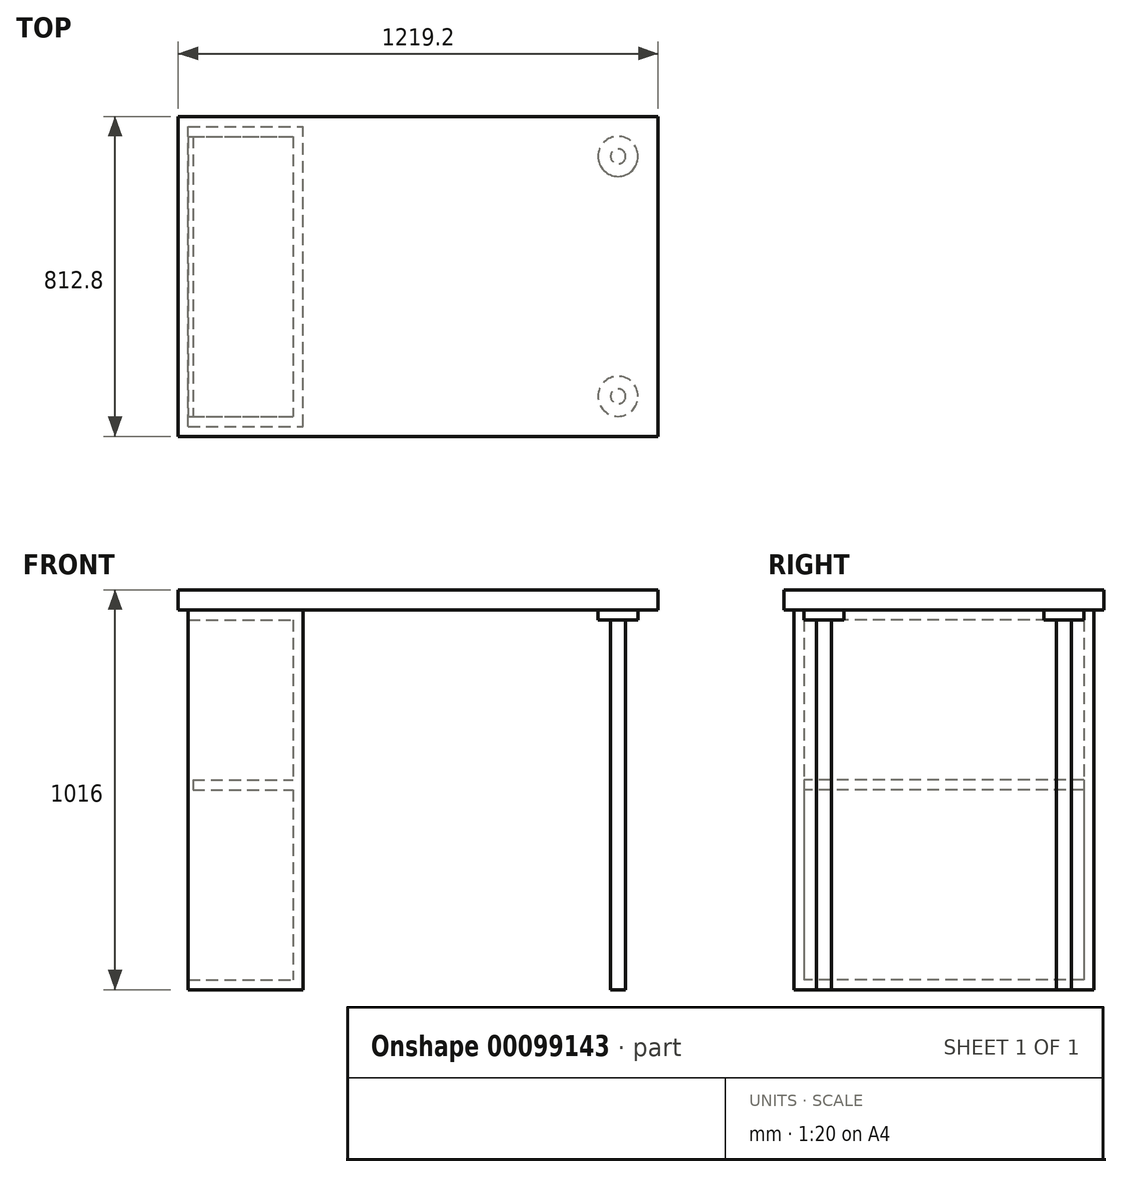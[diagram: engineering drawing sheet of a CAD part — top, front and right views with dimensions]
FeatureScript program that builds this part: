
annotation { "Feature Type Name" : "Feature", "Feature Type Description" : "" }
export const myFeature = defineFeature(function(context is Context, id is Id, definition is map)
    precondition{}
    {
        {
            var Q0;
            Q0=qCreatedBy(makeId("Top.planeOp"),FACE);
            var sketch = newSketch(context, id + "F0", { "sketchPlane" : qUnion([Q0])});
            skLineSegment(sketch, "E0.bottom", {"start": v(-704.9, -381) * mm, "end": v(-413.7, -381) * mm});
            skLineSegment(sketch, "E0.top", {"start": v(-704.9, 381) * mm, "end": v(-413.7, 381) * mm});
            skLineSegment(sketch, "E0.left", {"start": v(-704.9, -381) * mm, "end": v(-704.9, 381) * mm});
            skLineSegment(sketch, "E0.right", {"start": v(-413.7, -381) * mm, "end": v(-413.7, 381) * mm});
            skPoint(sketch, "E0.middle", {"position": v(-559.3, 0) * mm});
            skSolve(sketch);
        }
        {
            var Q0;
            Q0=makeQuery(id+"F0.imprint","IMPRINT",FACE,{"disambiguationData":[TD([[makeQuery(id+"F0.imprint","IMPRINT",EDGE,{"derivedFrom":sQuery(id+"F0.wireOp",EDGE,"E0.bottom")}),1.0]])]});
            extrude(context, id + "F1", {"entities" : qUnion([Q0]), "depth" : 25.4 * mm});
        }
        {
            var Q0;
            Q0=makeQuery(id+"F1.opExtrude","CAP_FACE",FACE,{"disambiguationData":[OSD([sQuery(id+"F0.wireOp",EDGE,"E0.bottom"),sQuery(id+"F0.wireOp",EDGE,"E0.top"),sQuery(id+"F0.wireOp",EDGE,"E0.left"),sQuery(id+"F0.wireOp",EDGE,"E0.right")])],"isStart":false});
            var sketch = newSketch(context, id + "F2", { "sketchPlane" : qUnion([Q0])});
            skLineSegment(sketch, "E1.bottom", {"start": v(-413.7, 381) * mm, "end": v(-439.1, 381) * mm});
            skLineSegment(sketch, "E1.top", {"start": v(-413.7, -381) * mm, "end": v(-439.1, -381) * mm});
            skLineSegment(sketch, "E1.left", {"start": v(-413.7, 381) * mm, "end": v(-413.7, -381) * mm});
            skLineSegment(sketch, "E1.right", {"start": v(-439.1, 381) * mm, "end": v(-439.1, -381) * mm});
            skLineSegment(sketch, "E2.bottom", {"start": v(-704.9, 381) * mm, "end": v(-439.1, 381) * mm});
            skLineSegment(sketch, "E2.top", {"start": v(-704.9, 355.6) * mm, "end": v(-439.1, 355.6) * mm});
            skLineSegment(sketch, "E2.left", {"start": v(-704.9, 381) * mm, "end": v(-704.9, 355.6) * mm});
            skLineSegment(sketch, "E2.right", {"start": v(-439.1, 381) * mm, "end": v(-439.1, 355.6) * mm});
            skLineSegment(sketch, "E3.bottom", {"start": v(-704.9, -381) * mm, "end": v(-439.1, -381) * mm});
            skLineSegment(sketch, "E3.top", {"start": v(-704.9, -355.6) * mm, "end": v(-439.1, -355.6) * mm});
            skLineSegment(sketch, "E3.left", {"start": v(-704.9, -381) * mm, "end": v(-704.9, -355.6) * mm});
            skLineSegment(sketch, "E3.right", {"start": v(-439.1, -381) * mm, "end": v(-439.1, -355.6) * mm});
            skSolve(sketch);
        }
        {
            var Q0;
            Q0=makeQuery(id+"F2.imprint","IMPRINT",FACE,{"disambiguationData":[TD([[makeQuery(id+"F2.imprint","IMPRINT",EDGE,{"derivedFrom":sQuery(id+"F2.wireOp",EDGE,"E1.bottom")}),-1.0]])]});
            var Q1;
            Q1=makeQuery(id+"F2.imprint","IMPRINT",FACE,{"disambiguationData":[TD([[makeQuery(id+"F2.imprint","IMPRINT",EDGE,{"derivedFrom":sQuery(id+"F2.wireOp",EDGE,"E2.bottom")}),-1.0]])]});
            var Q2;
            Q2=makeQuery(id+"F2.imprint","IMPRINT",FACE,{"disambiguationData":[TD([[makeQuery(id+"F2.imprint","IMPRINT",EDGE,{"derivedFrom":sQuery(id+"F2.wireOp",EDGE,"E3.bottom")}),1.0]])]});
            extrude(context, id + "F3", {"entities" : qUnion([Q0, Q1, Q2]), "operationType" : NewBodyOperationType.ADD, "depth" : 914.4 * mm});
        }
        {
            var Q0;
            Q0=makeQuery(id+"F3.opExtrude","CAP_FACE",FACE,{"disambiguationData":[OSD([sQuery(id+"F2.wireOp",EDGE,"E1.bottom"),sQuery(id+"F2.wireOp",EDGE,"E1.top"),sQuery(id+"F2.wireOp",EDGE,"E1.left"),sQuery(id+"F2.wireOp",EDGE,"E1.right"),sQuery(id+"F2.wireOp",EDGE,"E2.bottom"),sQuery(id+"F2.wireOp",EDGE,"E2.top"),sQuery(id+"F2.wireOp",EDGE,"E2.left"),sQuery(id+"F2.wireOp",EDGE,"E3.bottom"),sQuery(id+"F2.wireOp",EDGE,"E3.top"),sQuery(id+"F2.wireOp",EDGE,"E3.left")])],"isStart":false});
            cPlane(context, id + "F4", {"entities" : qUnion([Q0]), "cplaneType" : CPlaneType.OFFSET, "offset" : 0 * mm, "width" : 152.4 * mm, "height" : 152.4 * mm});
        }
        {
            var Q0;
            Q0=qCreatedBy(id+"F4.planeOp",FACE);
            var sketch = newSketch(context, id + "F5", { "sketchPlane" : qUnion([Q0])});
            skLineSegment(sketch, "E4.0.1", {"start": v(-704.9, 381) * mm, "end": v(-704.9, 355.6) * mm});
            skLineSegment(sketch, "E4.0.3", {"start": v(-439.1, 355.6) * mm, "end": v(-439.1, -355.6) * mm});
            skLineSegment(sketch, "E4.0.5", {"start": v(-704.9, -355.6) * mm, "end": v(-704.9, -381) * mm});
            skLineSegment(sketch, "E4.0.7", {"start": v(-413.7, -381) * mm, "end": v(-413.7, 381) * mm});
            skPoint(sketch, "E5.0", {"position": v(-704.9, 355.6) * mm});
            skPoint(sketch, "E6.0", {"position": v(-704.9, -381) * mm});
            skLineSegment(sketch, "E7.0.0", {"start": v(-413.7, 381) * mm, "end": v(-704.9, 381) * mm});
            skLineSegment(sketch, "E7.0.2", {"start": v(-704.9, 355.6) * mm, "end": v(-439.1, 355.6) * mm});
            skLineSegment(sketch, "E7.0.4", {"start": v(-439.1, -355.6) * mm, "end": v(-704.9, -355.6) * mm});
            skLineSegment(sketch, "E7.0.6", {"start": v(-704.9, -381) * mm, "end": v(-413.7, -381) * mm});
            skLineSegment(sketch, "E8.bottom", {"start": v(-704.9, 381) * mm, "end": v(-413.7, 381) * mm});
            skLineSegment(sketch, "E8.left", {"start": v(-704.9, 381) * mm, "end": v(-704.9, -381) * mm});
            skLineSegment(sketch, "E8.right", {"start": v(-413.7, 381) * mm, "end": v(-413.7, -381) * mm});
            skSolve(sketch);
        }
        {
            var Q0;
            {var subQ0=sQuery(id+"F5.wireOp",EDGE,"E7.0.2");Q0=makeQuery(id+"F5.imprint","IMPRINT",FACE,{"disambiguationData":[TD([[makeQuery(id+"F5.imprint","IMPRINT",EDGE,{"derivedFrom":subQ0}),-1.0]])]});}
            var Q1;
            {var subQ3=sQuery(id+"F5.wireOp",EDGE,"E7.0.2");Q1=makeQuery(id+"F5.imprint","IMPRINT",FACE,{"disambiguationData":[TD([[makeQuery(id+"F5.imprint","IMPRINT",EDGE,{"derivedFrom":subQ3}),1.0]])]});}
            extrude(context, id + "F6", {"entities" : qUnion([Q0, Q1]), "operationType" : NewBodyOperationType.ADD, "depth" : 25.4 * mm});
        }
        {
            var Q0;
            Q0=makeQuery(id+"F6.opExtrude","CAP_FACE",FACE,{"disambiguationData":[OSD([sQuery(id+"F5.wireOp",EDGE,"E8.bottom"),sQuery(id+"F5.wireOp",EDGE,"E7.0.6"),sQuery(id+"F5.wireOp",EDGE,"E8.left"),sQuery(id+"F5.wireOp",EDGE,"E8.right")])],"isStart":false});
            cPlane(context, id + "F7", {"entities" : qUnion([Q0]), "cplaneType" : CPlaneType.OFFSET, "offset" : 0 * mm, "width" : 152.4 * mm, "height" : 152.4 * mm});
        }
        {
            var Q0;
            Q0=qCreatedBy(id+"F7.planeOp",FACE);
            var sketch = newSketch(context, id + "F8", { "sketchPlane" : qUnion([Q0])});
            skLineSegment(sketch, "E9.0.0", {"start": v(-704.9, 381) * mm, "end": v(-704.9, -381) * mm});
            skLineSegment(sketch, "E9.0.1", {"start": v(-704.9, -381) * mm, "end": v(-413.7, -381) * mm});
            skLineSegment(sketch, "E9.0.2", {"start": v(-413.7, -381) * mm, "end": v(-413.7, 381) * mm});
            skLineSegment(sketch, "E9.0.3", {"start": v(-413.7, 381) * mm, "end": v(-704.9, 381) * mm});
            skPoint(sketch, "E10", {"position": v(-730.3, 406.4) * mm});
            skPoint(sketch, "E11", {"position": v(-730.3, -406.4) * mm});
            skPoint(sketch, "E12", {"position": v(-730.3, -381) * mm});
            skPoint(sketch, "E13", {"position": v(-730.3, 381) * mm});
            skLineSegment(sketch, "E14.bottom", {"start": v(-730.3, 406.4) * mm, "end": v(488.9, 406.4) * mm});
            skLineSegment(sketch, "E14.top", {"start": v(-730.3, -406.4) * mm, "end": v(488.9, -406.4) * mm});
            skLineSegment(sketch, "E14.left", {"start": v(-730.3, 406.4) * mm, "end": v(-730.3, -406.4) * mm});
            skLineSegment(sketch, "E14.right", {"start": v(488.9, 406.4) * mm, "end": v(488.9, -406.4) * mm});
            skSolve(sketch);
        }
        {
            var Q0;
            Q0=makeQuery(id+"F8.imprint","IMPRINT",FACE,{"disambiguationData":[TD([[makeQuery(id+"F8.imprint","IMPRINT",EDGE,{"derivedFrom":sQuery(id+"F8.wireOp",EDGE,"E9.0.0")}),-1.0]])]});
            var Q1;
            Q1=makeQuery(id+"F8.imprint","IMPRINT",FACE,{"disambiguationData":[TD([[makeQuery(id+"F8.imprint","IMPRINT",EDGE,{"derivedFrom":sQuery(id+"F8.wireOp",EDGE,"E9.0.0")}),1.0]])]});
            extrude(context, id + "F9", {"entities" : qUnion([Q0, Q1]), "depth" : 50.8 * mm});
        }
        {
            var Q0;
            Q0=makeQuery(id+"F9.opExtrude","CAP_FACE",FACE,{"disambiguationData":[OSD([sQuery(id+"F8.wireOp",EDGE,"E14.bottom"),sQuery(id+"F8.wireOp",EDGE,"E14.top"),sQuery(id+"F8.wireOp",EDGE,"E14.left"),sQuery(id+"F8.wireOp",EDGE,"E14.right")])],"isStart":true});
            var sketch = newSketch(context, id + "F10", { "sketchPlane" : qUnion([Q0])});
            skPoint(sketch, "E15", {"position": v(387.3, 304.8) * mm});
            skCircle(sketch, "E16", {"center": v(387.3, 304.8) * mm, "radius": 50.8 * mm});
            skSolve(sketch);
        }
        {
            var Q0;
            Q0=makeQuery(id+"F10.imprint","IMPRINT",FACE,{"disambiguationData":[TD([[makeQuery(id+"F10.imprint","IMPRINT",EDGE,{"derivedFrom":sQuery(id+"F10.wireOp",EDGE,"E16")}),1.0]])]});
            var Q1;
            Q1=makeQuery(id+"F10.imprint","IMPRINT",FACE,{"disambiguationData":[TD([[makeQuery(id+"F10.imprint","IMPRINT",EDGE,{"derivedFrom":sQuery(id+"F10.wireOp",EDGE,"xEtVv1aL-S2a0-IO3G-oLLT-fGSTPTcQIMz1")}),1.0]])]});
            extrude(context, id + "F11", {"entities" : qUnion([Q0, Q1]), "depth" : 25.4 * mm});
        }
        {
            var Q0;
            Q0=makeQuery(id+"F11.opExtrude","CAP_FACE",FACE,{"disambiguationData":[OSD([sQuery(id+"F10.wireOp",EDGE,"E16")])],"isStart":false});
            var sketch = newSketch(context, id + "F12", { "sketchPlane" : qUnion([Q0])});
            skCircle(sketch, "E17", {"center": v(387.3, 304.8) * mm, "radius": 19.05 * mm});
            skSolve(sketch);
        }
        {
            var Q0;
            Q0=makeQuery(id+"F12.imprint","IMPRINT",FACE,{"disambiguationData":[TD([[makeQuery(id+"F12.imprint","IMPRINT",EDGE,{"derivedFrom":sQuery(id+"F12.wireOp",EDGE,"E17")}),1.0]])]});
            extrude(context, id + "F13", {"entities" : qUnion([Q0]), "operationType" : NewBodyOperationType.ADD, "depth" : 939.8 * mm});
        }
        {
            var Q0;
            Q0=makeQuery(id+"F9.opExtrude","CAP_FACE",FACE,{"disambiguationData":[OSD([sQuery(id+"F8.wireOp",EDGE,"E14.bottom"),sQuery(id+"F8.wireOp",EDGE,"E14.top"),sQuery(id+"F8.wireOp",EDGE,"E14.left"),sQuery(id+"F8.wireOp",EDGE,"E14.right")])],"isStart":true});
            var sketch = newSketch(context, id + "F14", { "sketchPlane" : qUnion([Q0])});
            skLineSegment(sketch, "E18", {"start": v(488.9, 0) * mm, "end": v(-730.3, 0) * mm, "construction": true});
            skSolve(sketch);
        }
        {
            var Q0;
            Q0=sQuery(id+"F14.wireOp",EDGE,"E18");
            cPlane(context, id + "F15", {"entities" : qUnion([Q0]), "cplaneType" : CPlaneType.LINE_ANGLE, "offset" : 152.4 * mm, "angle" : 180 * degree, "width" : 152.4 * mm, "height" : 152.4 * mm});
        }
        {
            var Q0;
            Q0=makeQuery(id+"F11.opExtrude","SWEPT_BODY",BODY,{"disambiguationData":[OSD([sQuery(id+"F10.wireOp",EDGE,"E16")])]});
            var Q1;
            Q1=qCreatedBy(id+"F15.planeOp",FACE);
            mirror(context, id + "F16", {"operationType" : NewBodyOperationType.ADD, "entities" : qUnion([Q0]), "mirrorPlane" : qUnion([Q1])});
        }
        {
            var Q0;
            Q0=makeQuery(id+"F3.opExtrude","SWEPT_FACE",FACE,{"disambiguationData":[OSD([sQuery(id+"F2.wireOp",EDGE,"E1.right")])]});
            var sketch = newSketch(context, id + "F17", { "sketchPlane" : qUnion([Q0])});
            skLineSegment(sketch, "E19.bottom", {"start": v(-355.6, 533.4) * mm, "end": v(355.6, 533.4) * mm});
            skLineSegment(sketch, "E19.top", {"start": v(-355.6, 508) * mm, "end": v(355.6, 508) * mm});
            skLineSegment(sketch, "E19.left", {"start": v(-355.6, 533.4) * mm, "end": v(-355.6, 508) * mm});
            skLineSegment(sketch, "E19.right", {"start": v(355.6, 533.4) * mm, "end": v(355.6, 508) * mm});
            skSolve(sketch);
        }
        {
            var Q0;
            Q0=makeQuery(id+"F17.imprint","IMPRINT",FACE,{"disambiguationData":[TD([[makeQuery(id+"F17.imprint","IMPRINT",EDGE,{"derivedFrom":sQuery(id+"F17.wireOp",EDGE,"E19.bottom")}),-1.0]])]});
            extrude(context, id + "F18", {"entities" : qUnion([Q0]), "operationType" : NewBodyOperationType.ADD, "depth" : 254 * mm});
        }
    });
